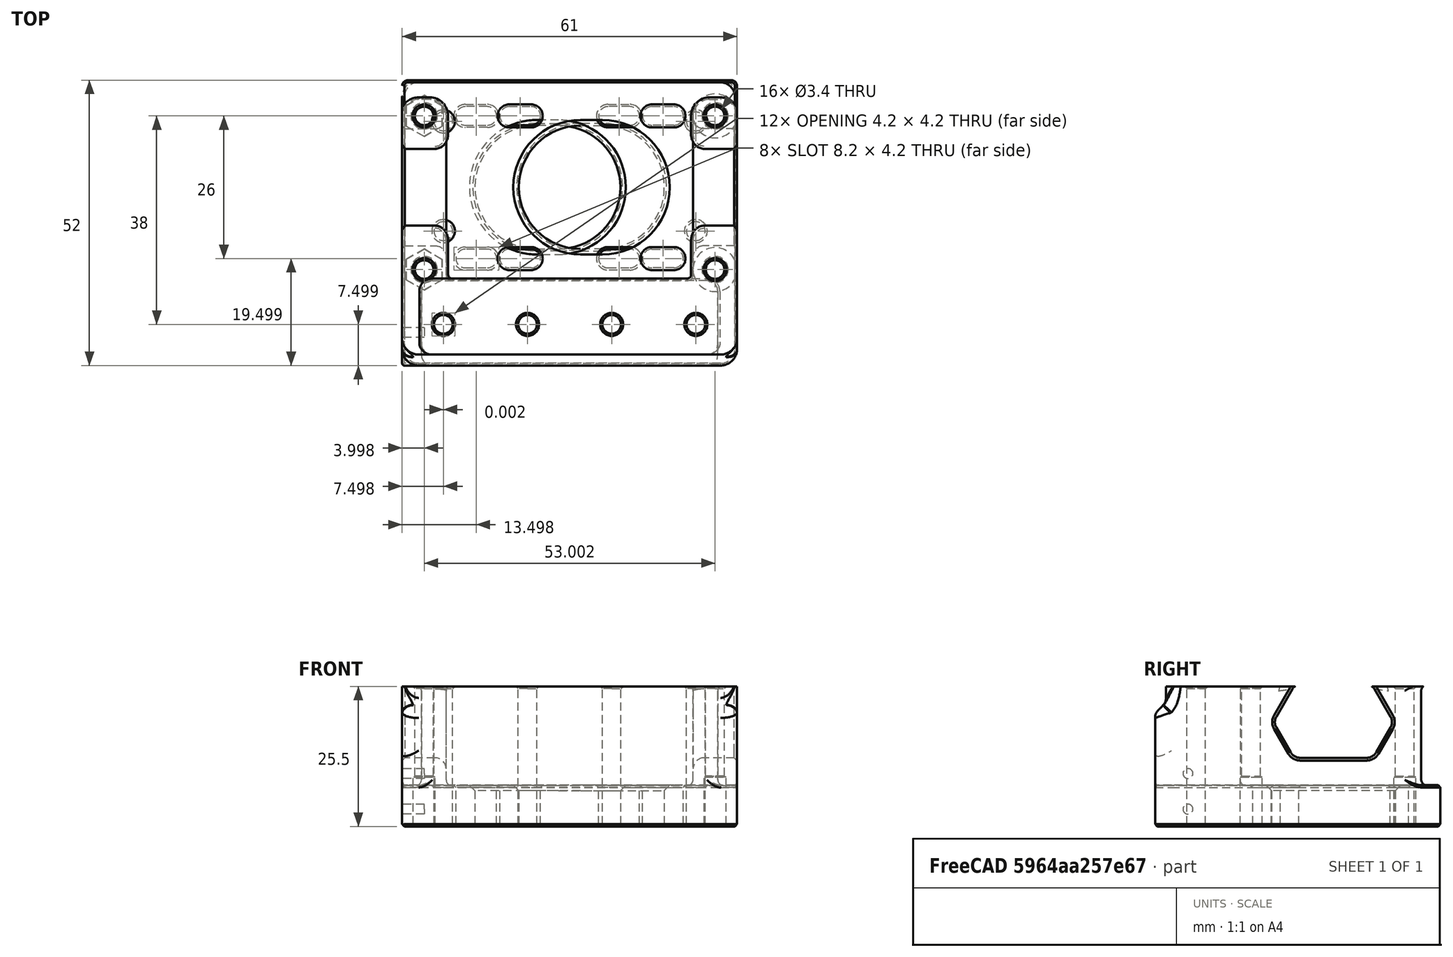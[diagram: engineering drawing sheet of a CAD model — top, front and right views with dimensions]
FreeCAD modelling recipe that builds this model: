
FCSTD DOCUMENT  (FreeCAD 0.18R16146 (Git))
Label: AB-motor-mount
License: All rights reserved
LicenseURL: http://en.wikipedia.org/wiki/All_rights_reserved
objects: Part::Cylinder×8, Part::MultiFuse×6, Part::Cut×5, Part::Box×4, Part::Chamfer×4, Part::Feature×2
note: 29 computed .brp shape members not serialized (recipe doc carries the construction recipe); baked Part::Feature solids carry a one-line shape summary decoded from their .brp

FEATURE [Part::Feature] Part__Feature297  label="B_Drive_Frame"
  Placement = pos=(30.5001,25.9989,0.00249282) rot=(0,0.707107,0.707107;3.14159rad)
  shape: bbox 63.11 x 54.03 x 28.1 mm, 230 faces (baked)
FEATURE [Part::Feature] Part__Feature846  label="A_Drive_Frame003"
  Placement = pos=(-30.5017,25.9989,-0.00214308) rot=(0,0.707107,0.707107;3.14159rad)
  shape: bbox 63.1 x 54.1 x 28.1 mm, 238 faces (baked)
FEATURE [Part::Cylinder] Cylinder
  Angle = 360
  AttacherType = Attacher::AttachEngine3D
  Height = 6.5
  Placement = pos=(57,17.5,0) rot=(0,0,1;0rad)
  Radius = 4
FEATURE [Part::Cylinder] Cylinder001
  Angle = 360
  AttacherType = Attacher::AttachEngine3D
  Height = 9
  Placement = pos=(4,17.5,0) rot=(0,0,1;0rad)
  Radius = 2
FEATURE [Part::Cylinder] Cylinder002
  Angle = 360
  AttacherType = Attacher::AttachEngine3D
  Height = 9
  Placement = pos=(4,45.5,0) rot=(0,0,1;0rad)
  Radius = 2
FEATURE [Part::Cylinder] Cylinder003
  Angle = 360
  AttacherType = Attacher::AttachEngine3D
  Height = 6.5
  Placement = pos=(57,45.5,0) rot=(0,0,1;0rad)
  Radius = 4
FEATURE [Part::Box] Box  label="Cube"
  AttacherType = Attacher::AttachEngine3D
  Height = 10
  Length = 10
  Placement = pos=(60.6,13,0) rot=(0,0,1;0rad)
  Width = 10
FEATURE [Part::Box] Box001  label="Cube001"
  AttacherType = Attacher::AttachEngine3D
  Height = 10
  Length = 10
  Placement = pos=(60.6,41,0) rot=(0,0,1;0rad)
  Width = 10
FEATURE [Part::Cylinder] Cylinder004
  Angle = 360
  AttacherType = Attacher::AttachEngine3D
  Height = 9
  Placement = pos=(57,17.5,0) rot=(0,0,1;0rad)
  Radius = 2
FEATURE [Part::Cylinder] Cylinder005
  Angle = 360
  AttacherType = Attacher::AttachEngine3D
  Height = 9
  Placement = pos=(57,45.5,0) rot=(0,0,1;0rad)
  Radius = 2
FEATURE [Part::Cut] Cut
  Base = -> Cylinder003
  Tool = -> Box001
FEATURE [Part::Cut] Cut001
  Base = -> Cylinder
  Tool = -> Box
FEATURE [Part::MultiFuse] Fusion
  Shapes = -> [Cut001,Cut,Part__Feature297]
FEATURE [Part::Box] Box002  label="Cube002"
  AttacherType = Attacher::AttachEngine3D
  Height = 10
  Length = 10
  Placement = pos=(-9.6,13,0) rot=(0,0,1;0rad)
  Width = 10
FEATURE [Part::Box] Box003  label="Cube003"
  AttacherType = Attacher::AttachEngine3D
  Height = 10
  Length = 10
  Placement = pos=(-9.6,41,0) rot=(0,0,1;0rad)
  Width = 10
FEATURE [Part::Cylinder] Cylinder006
  Angle = 360
  AttacherType = Attacher::AttachEngine3D
  Height = 6.5
  Placement = pos=(4,45.5,0) rot=(0,0,1;0rad)
  Radius = 4
FEATURE [Part::Cylinder] Cylinder007
  Angle = 360
  AttacherType = Attacher::AttachEngine3D
  Height = 6.5
  Placement = pos=(4,17.5,0) rot=(0,0,1;0rad)
  Radius = 4
FEATURE [Part::MultiFuse] Fusion002
  Shapes = -> [Cylinder007,Cylinder006]
FEATURE [Part::MultiFuse] Fusion003
  Shapes = -> [Box003,Box002]
FEATURE [Part::Cut] Cut003
  Base = -> Fusion002
  Tool = -> Fusion003
FEATURE [Part::MultiFuse] Fusion004
  Shapes = -> [Cut003,Part__Feature846]
FEATURE [Part::MultiFuse] Fusion006
  Shapes = -> [Cylinder005,Cylinder004]
FEATURE [Part::Cut] Cut005
  Base = -> Fusion
  Tool = -> Fusion006
FEATURE [Part::Chamfer] Chamfer001
  Base = -> Cut005
  Edges = 2 edges r=0.2: [Edge32,Edge489]
FEATURE [Part::Chamfer] Chamfer002
  Base = -> Chamfer001
  Edges = 2 edges r=0.4: [Edge38,Edge522]
FEATURE [Part::MultiFuse] Fusion007
  Shapes = -> [Cylinder001,Cylinder002]
FEATURE [Part::Cut] Cut006
  Base = -> Fusion004
  Tool = -> Fusion007
FEATURE [Part::Chamfer] Chamfer
  Base = -> Cut006
  Edges = 2 edges r=0.2: [Edge441,Edge466]
FEATURE [Part::Chamfer] Chamfer003
  Base = -> Chamfer
  Edges = 2 edges r=0.4: [Edge38,Edge548]
